# Revit family: Haworth_TateColor_Stool
name_source: partatom
category: Furniture
revit_build: Autodesk Revit 2018 (Build: 20170223_1515(x64)
units: mm (PartAtom-declared; Revit-internal decimal feet)

## family parameters
Always vertical = Yes
Cut with Voids When Loaded = No
OmniClass Number = 23.40.70.14.64.11
OmniClass Title = Office Furniture
Room Calculation Point = No
Shared = No
Work Plane-Based = No

## types (4) — shared parameters
Actual Depth = 18"
Actual Width = 20"
Assembly Code = E2020200
Description = Haworth Tate Color Stool
Glide Finish = Haworth _ Paint _ Collection White
Manufacturer = Haworth
Model = HCCE-TC
Revision Number = 4
URL = http://www.haworth.com
URL - Product = http://www.haworth.com
Warranty = http://www.haworth.com

## per-type parameters (varying)
| type | Actual Height | High | High Back | Low | Low Back | Low Seat Height |
| HCCE-TC - Low Stool - Low Back | 39 5/8" | No | No | Yes | Yes | 22 7/8" |
| HCCE-TC - High Stool - Low Back | 45 7/8" | Yes | No | No | Yes | 29 1/4" |
| HCCE-TC - Low Stool - High Back | 39 5/8" | No | Yes | Yes | No | 22 7/8" |
| HCCE-TC - High Stool - High Back | 45 7/8" | Yes | Yes | No | No | 29 1/4" |

## geometry (parser evidence)
native form markers: Sweep x13
no freeform markers — native parametric forms only
